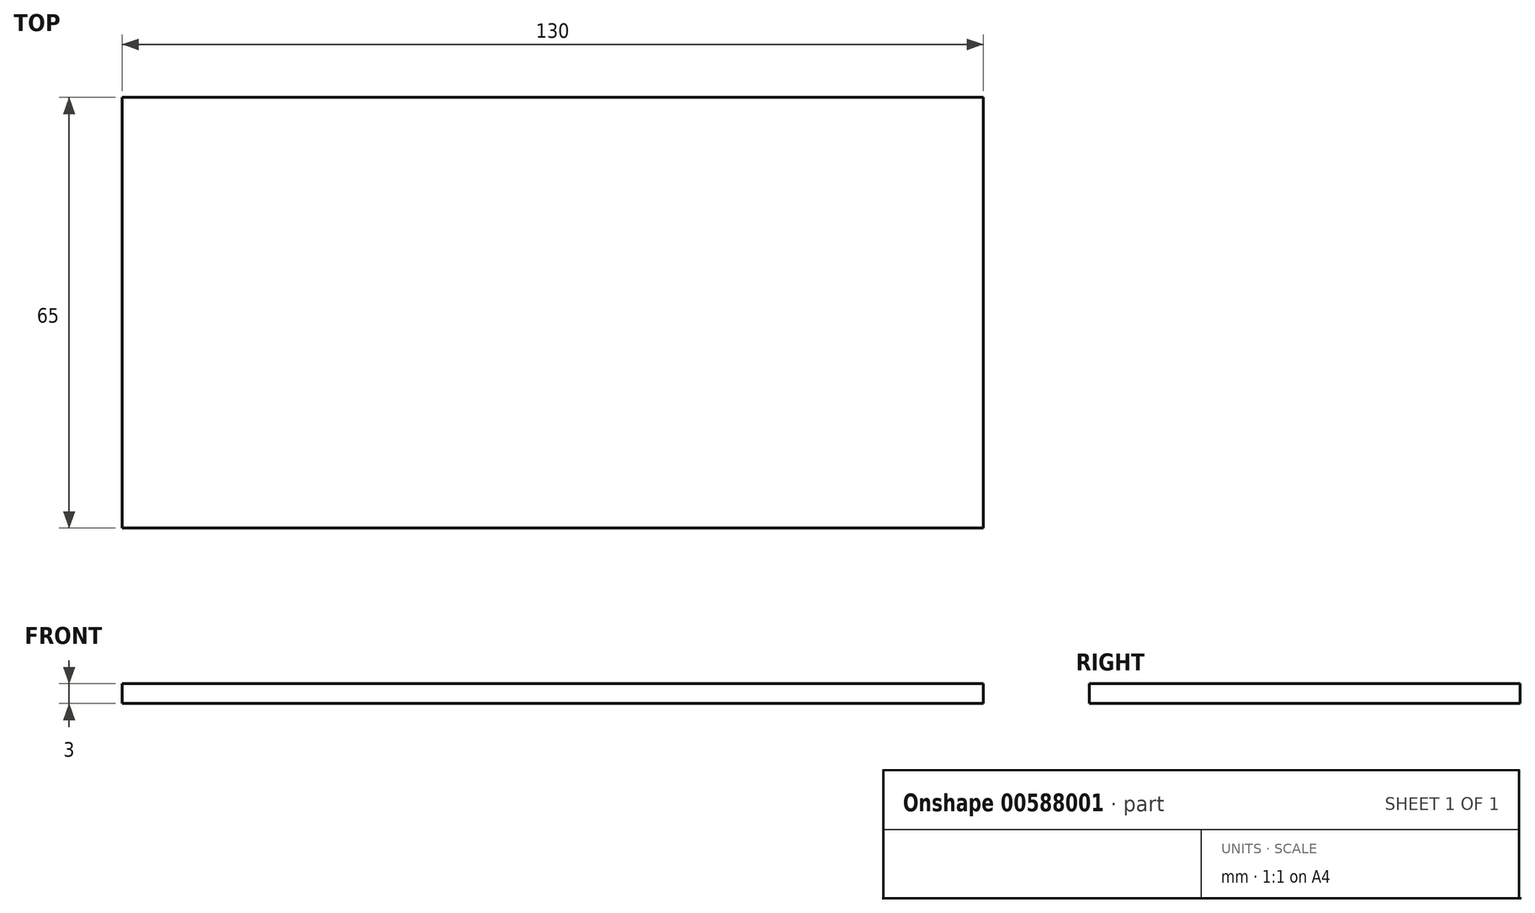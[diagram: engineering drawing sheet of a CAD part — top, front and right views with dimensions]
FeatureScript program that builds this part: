
annotation { "Feature Type Name" : "Feature", "Feature Type Description" : "" }
export const myFeature = defineFeature(function(context is Context, id is Id, definition is map)
    precondition{}
    {
        {
            var Q0;
            Q0=qCreatedBy(makeId("Top.planeOp"),FACE);
            var sketch = newSketch(context, id + "F0", { "sketchPlane" : qUnion([Q0])});
            skLineSegment(sketch, "E0.bottom", {"start": v(65, 32.5) * mm, "end": v(-65, 32.5) * mm});
            skLineSegment(sketch, "E0.top", {"start": v(65, -32.5) * mm, "end": v(-65, -32.5) * mm});
            skLineSegment(sketch, "E0.left", {"start": v(65, 32.5) * mm, "end": v(65, -32.5) * mm});
            skLineSegment(sketch, "E0.right", {"start": v(-65, 32.5) * mm, "end": v(-65, -32.5) * mm});
            skPoint(sketch, "E0.middle", {"position": v(0, 0) * mm});
            skSolve(sketch);
        }
        {
            var Q0;
            Q0=makeQuery(id+"F0.imprint","IMPRINT",FACE,{"disambiguationData":[TD([[makeQuery(id+"F0.imprint","IMPRINT",EDGE,{"derivedFrom":sQuery(id+"F0.wireOp",EDGE,"E0.bottom")}),1.0]])]});
            extrude(context, id + "F1", {"entities" : qUnion([Q0]), "depth" : 3 * mm, "offsetDistance" : 25 * mm});
        }
    });
